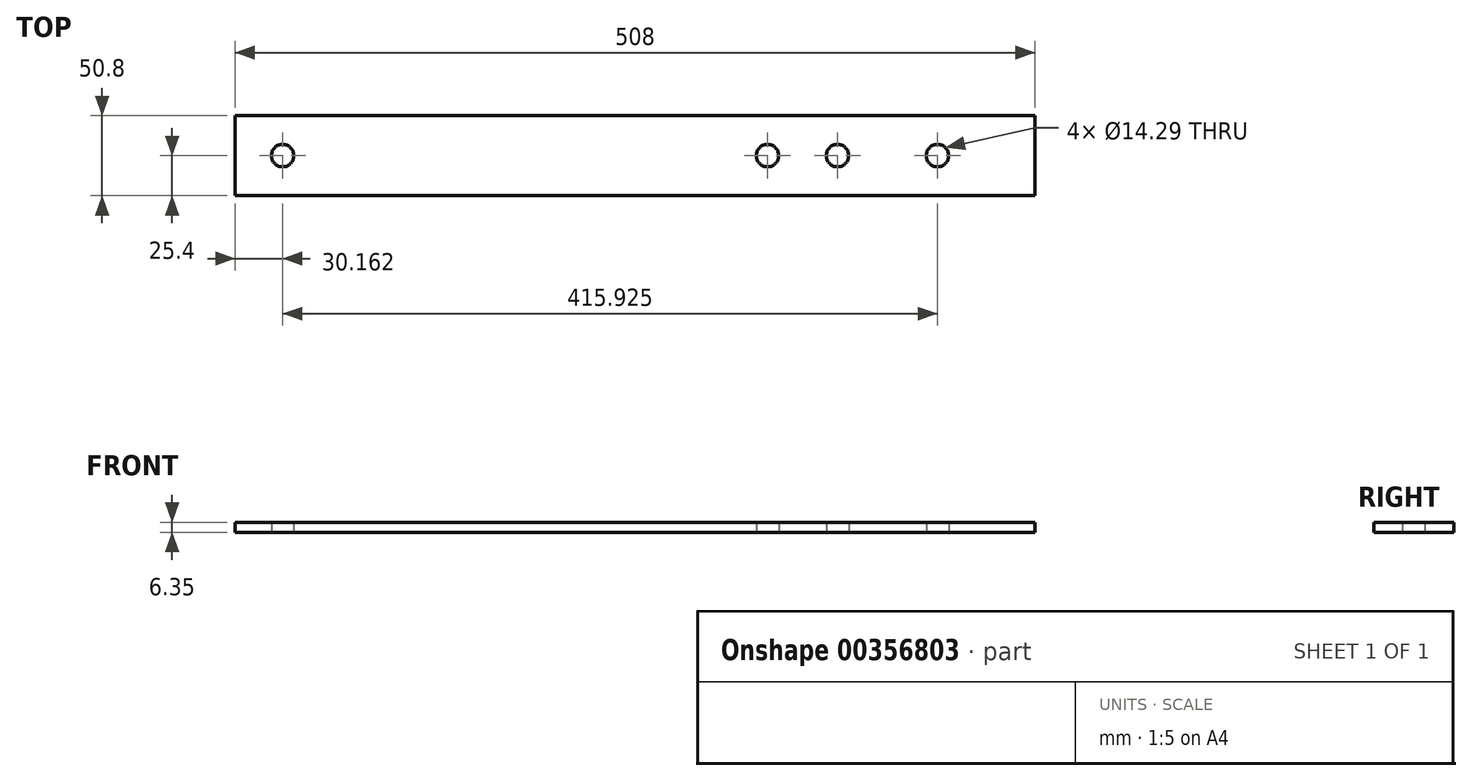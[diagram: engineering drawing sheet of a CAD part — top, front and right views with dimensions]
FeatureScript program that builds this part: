
annotation { "Feature Type Name" : "Feature", "Feature Type Description" : "" }
export const myFeature = defineFeature(function(context is Context, id is Id, definition is map)
    precondition{}
    {
        {
            var Q0;
            Q0=qCreatedBy(makeId("Top.planeOp"),FACE);
            var sketch = newSketch(context, id + "F0", { "sketchPlane" : qUnion([Q0])});
            skLineSegment(sketch, "E0.bottom", {"start": v(254, -25.4) * mm, "end": v(-254, -25.4) * mm});
            skLineSegment(sketch, "E0.top", {"start": v(254, 25.4) * mm, "end": v(-254, 25.4) * mm});
            skLineSegment(sketch, "E0.left", {"start": v(254, -25.4) * mm, "end": v(254, 25.4) * mm});
            skLineSegment(sketch, "E0.right", {"start": v(-254, -25.4) * mm, "end": v(-254, 25.4) * mm});
            skPoint(sketch, "E0.middle", {"position": v(0, 0) * mm});
            skCircle(sketch, "E1", {"center": v(-223.84, 0) * mm, "radius": 7.14 * mm});
            skCircle(sketch, "E2", {"center": v(192.09, 0) * mm, "radius": 7.14 * mm});
            skCircle(sketch, "E3", {"center": v(128.59, 0) * mm, "radius": 7.14 * mm});
            skCircle(sketch, "E4", {"center": v(84.12, 0) * mm, "radius": 7.14 * mm});
            skSolve(sketch);
        }
        {
            var Q0;
            Q0 = qSketchRegion(id + "F0", true);
            extrude(context, id + "F1", {"entities" : qUnion([Q0]), "depth" : 6.35 * mm});
        }
    });
